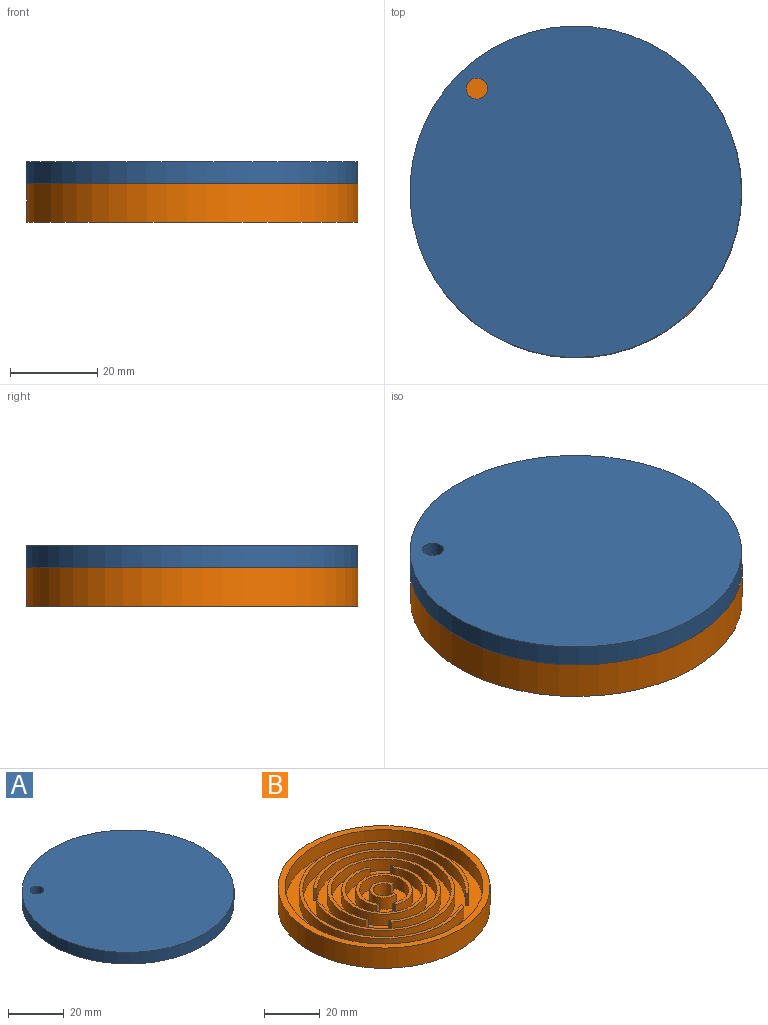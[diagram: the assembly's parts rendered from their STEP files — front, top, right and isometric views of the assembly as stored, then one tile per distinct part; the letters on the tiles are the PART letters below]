
ASSEMBLY  parts=2 mates=1
PART A: 4 faces, bbox 76.2x76.2x5.1 mm
  f0: cylinder r=2.41mm len=5.08mm, axis (0,0,-1), area 77mm2, adj f2,f3
  f1: cylinder r=38.1mm len=76.2mm, axis (0,0,-1), area 1216.1mm2, adj f2,f3
  f2: plane 76.2x76.2mm, normal (0,0,1), area 4542.1mm2, adj f0,f1
  f3: plane 76.2x76.2mm, normal (0,0,-1), area 4542.1mm2, adj f0,f1
PART B: 35 faces, bbox 76.2x76.2x8.9 mm
  f0: plane 71.12x71.12mm, normal (0,0,1), area 3164.5mm2, adj f4,f5,f6,f7,f8,f10,f11,f12
  f1: cylinder r=38.1mm len=76.2mm, axis (0,0,-1), area 2128.2mm2, adj f2,f3
  f2: plane 76.2x76.2mm, normal (0,0,1), area 587.8mm2, adj f1,f4
  f3: plane 76.2x76.2mm, normal (0,0,-1), area 4514.8mm2, adj f1,f30
  f4: cylinder r=35.56mm len=71.12mm, axis (0,0,-1), area 1418.8mm2, adj f0,f2
  f5: plane 5.08x1.41mm, normal (1,0,0), area 7.2mm2, adj f0,f6,f8,f9
  f6: cylinder r=29.21mm len=58.42mm, axis (0,0,-1), area 896.1mm2, adj f0,f5,f7,f9
  f7: plane 5.08x1.12mm, normal (-0.87,-0.5,0), area 6.6mm2, adj f0,f6,f8,f9
  f8: cylinder r=30.48mm len=60.96mm, axis (0,0,-1), area 933.1mm2, adj f0,f5,f7,f9
  f9: plane 60.96x60.96mm, normal (0,0,1), area 228.7mm2, adj f5,f6,f7,f8
  f10: plane 5.08x1.01mm, normal (-0.79,-0.61,0), area 6.5mm2, adj f0,f11,f13,f14
  f11: cylinder r=24.13mm len=48.26mm, axis (0,0,-1), area 718.8mm2, adj f0,f10,f12,f14
  f12: plane 5.08x2.95mm, normal (1,0,0), area 15mm2, adj f0,f11,f13,f14
  f13: cylinder r=25.4mm len=50.8mm, axis (0,0,-1), area 769.8mm2, adj f0,f10,f12,f14
  f14: plane 50.8x50.8mm, normal (0,0,1), area 186.1mm2, adj f10,f11,f12,f13
  f15: plane 5.08x1.42mm, normal (-0.01,-1,0), area 7.2mm2, adj f0,f16,f18,f19
  f16: cylinder r=19.05mm len=38.1mm, axis (0,0,-1), area 569.7mm2, adj f0,f15,f17,f19
  f17: plane 5.08x1.62mm, normal (-1,0,0), area 8.2mm2, adj f0,f16,f18,f19
  f18: cylinder r=20.32mm len=40.64mm, axis (0,0,-1), area 599mm2, adj f0,f15,f17,f19
  f19: plane 40.64x40.64mm, normal (0,0,1), area 146.1mm2, adj f15,f16,f17,f18
  f20: cylinder r=15.24mm len=30.48mm, axis (0,0,-1), area 444.3mm2, adj f0,f21,f23,f24
  f21: plane 5.08x2.32mm, normal (-1,0,0), area 11.8mm2, adj f0,f20,f22,f24
  f22: cylinder r=13.97mm len=27.94mm, axis (0,0,-1), area 400.4mm2, adj f0,f21,f23,f24
  f23: plane 5.08x1.38mm, normal (1,0,0), area 7mm2, adj f0,f20,f22,f24
  f24: plane 30.48x30.48mm, normal (0,0,1), area 105.6mm2, adj f20,f21,f22,f23
  f25: plane 5.08x1.49mm, normal (0,-1,0), area 7.5mm2, adj f0,f26,f28,f29
  f26: cylinder r=8.89mm len=17.78mm, axis (0,0,-1), area 258.4mm2, adj f0,f25,f27,f29
  f27: plane 5.08x1.38mm, normal (-1,0,0), area 7mm2, adj f0,f26,f28,f29
  f28: cylinder r=10.16mm len=20.32mm, axis (0,0,-1), area 288.3mm2, adj f0,f25,f27,f29
  f29: plane 20.32x20.32mm, normal (0,0,1), area 68.3mm2, adj f25,f26,f27,f28
  f30: cylinder r=3.81mm len=7.62mm, axis (0,0,-1), area 156.2mm2, adj f0,f3,f31,f33,f34
  f31: plane 5.08x1.27mm, normal (0,-1,0), area 6.5mm2, adj f0,f30,f32,f34
  f32: cylinder r=5.08mm len=10.16mm, axis (0,0,-1), area 125.8mm2, adj f0,f31,f33,f34
  f33: plane 5.08x1.32mm, normal (1,0,0), area 6.7mm2, adj f0,f30,f32,f34
  f34: plane 10.16x10.15mm, normal (0,0,1), area 27.7mm2, adj f30,f31,f32,f33
PLACE A t=(62.29,59.67,33.02)mm
PLACE B t=(62.38,59.58,24.13)mm
MATE fastened B.f1 <-> A.f3  axis (0,0,1) through (62.38,59.58,33.02)mm
